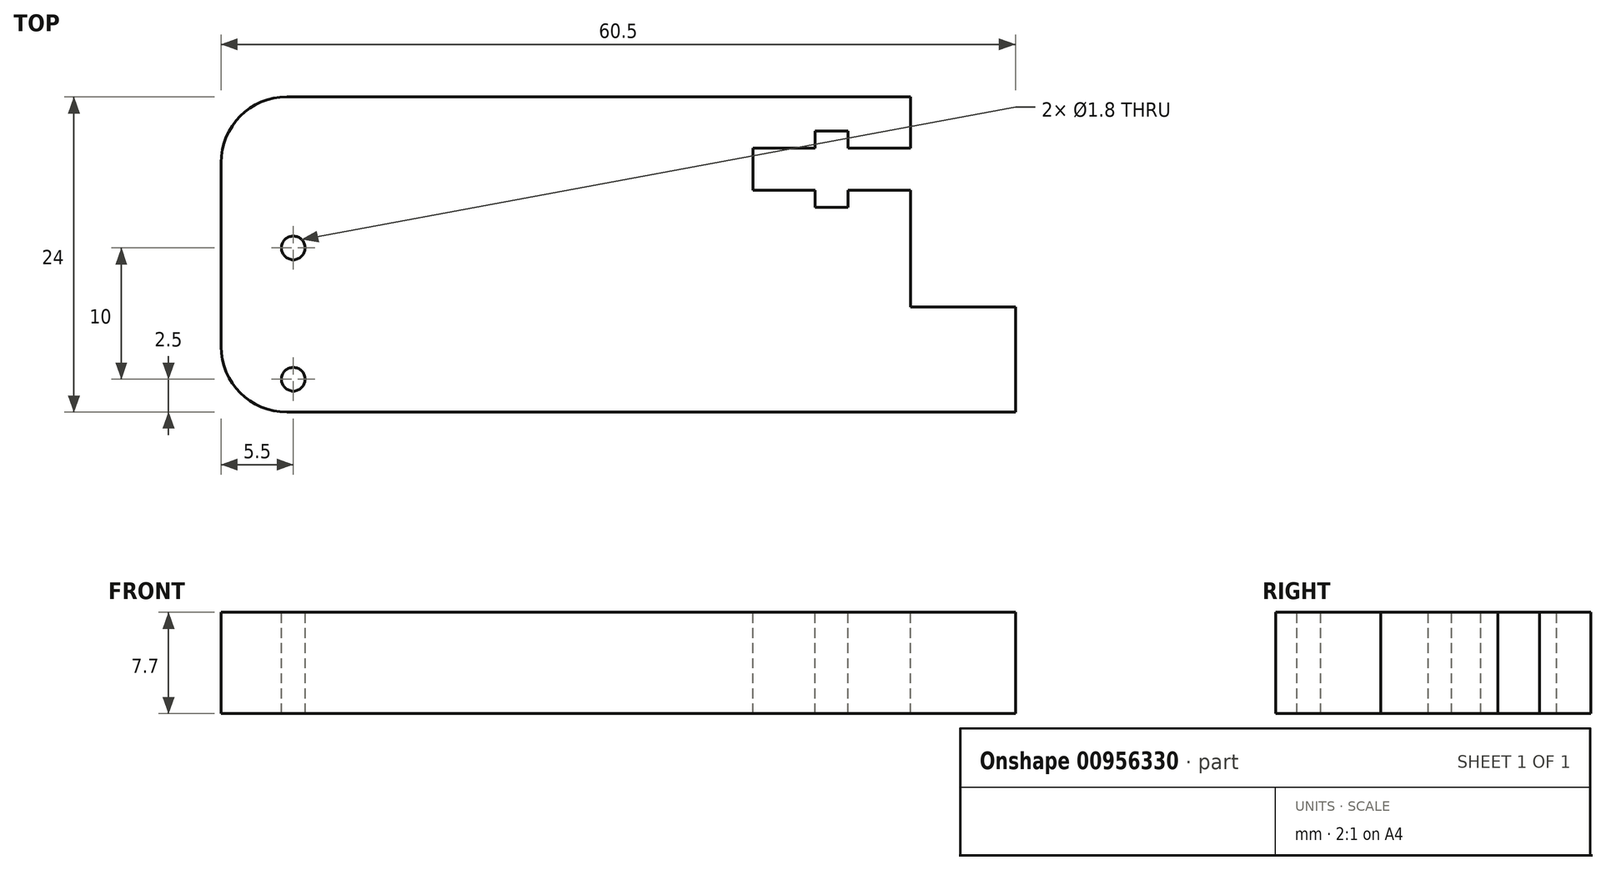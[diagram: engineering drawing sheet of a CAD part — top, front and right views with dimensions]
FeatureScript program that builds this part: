
annotation { "Feature Type Name" : "Feature", "Feature Type Description" : "" }
export const myFeature = defineFeature(function(context is Context, id is Id, definition is map)
    precondition{}
    {
        {
            var Q0;
            Q0=qCreatedBy(makeId("Top.planeOp"),FACE);
            var sketch = newSketch(context, id + "F0", { "sketchPlane" : qUnion([Q0])});
            skLineSegment(sketch, "E0", {"start": v(0, 0) * mm, "end": v(0, -8) * mm});
            skLineSegment(sketch, "E1", {"start": v(0, -8) * mm, "end": v(-60.5, -8) * mm});
            skLineSegment(sketch, "E2", {"start": v(-60.5, -8) * mm, "end": v(-60.5, 16) * mm});
            skLineSegment(sketch, "E3", {"start": v(-60.5, 16) * mm, "end": v(-8, 16) * mm});
            skLineSegment(sketch, "E4", {"start": v(-8, 16) * mm, "end": v(-8, 0) * mm});
            skLineSegment(sketch, "E5", {"start": v(-8, 0) * mm, "end": v(0, 0) * mm});
            skSolve(sketch);
        }
        {
            var Q0;
            Q0=makeQuery(id+"F0.imprint","IMPRINT",FACE,{"disambiguationData":[TD([[makeQuery(id+"F0.imprint","IMPRINT",EDGE,{"derivedFrom":sQuery(id+"F0.wireOp",EDGE,"E0")}),-1.0]])]});
            extrude(context, id + "F1", {"entities" : qUnion([Q0]), "depth" : 7.7 * mm, "offsetDistance" : 25 * mm});
        }
        {
            var Q0;
            Q0=makeQuery(id+"F1.opExtrude","CAP_FACE",FACE,{"disambiguationData":[OSD([sQuery(id+"F0.wireOp",EDGE,"E0"),sQuery(id+"F0.wireOp",EDGE,"E1"),sQuery(id+"F0.wireOp",EDGE,"E2"),sQuery(id+"F0.wireOp",EDGE,"E3"),sQuery(id+"F0.wireOp",EDGE,"E4"),sQuery(id+"F0.wireOp",EDGE,"E5")])],"isStart":false});
            var sketch = newSketch(context, id + "F2", { "sketchPlane" : qUnion([Q0])});
            skLineSegment(sketch, "E6", {"start": v(-8, 8.9) * mm, "end": v(-12.75, 8.9) * mm});
            skLineSegment(sketch, "E7", {"start": v(-12.75, 8.9) * mm, "end": v(-12.75, 7.6) * mm});
            skLineSegment(sketch, "E8", {"start": v(-12.75, 7.6) * mm, "end": v(-15.25, 7.6) * mm});
            skLineSegment(sketch, "E9", {"start": v(-15.25, 7.6) * mm, "end": v(-15.25, 8.9) * mm});
            skLineSegment(sketch, "E10", {"start": v(-15.25, 8.9) * mm, "end": v(-20, 8.9) * mm});
            skLineSegment(sketch, "E11", {"start": v(-20, 8.9) * mm, "end": v(-20, 12.1) * mm});
            skLineSegment(sketch, "E12", {"start": v(-20, 12.1) * mm, "end": v(-15.25, 12.1) * mm});
            skLineSegment(sketch, "E13", {"start": v(-15.25, 12.1) * mm, "end": v(-15.25, 13.4) * mm});
            skLineSegment(sketch, "E14", {"start": v(-15.25, 13.4) * mm, "end": v(-12.75, 13.4) * mm});
            skLineSegment(sketch, "E15", {"start": v(-12.75, 13.4) * mm, "end": v(-12.75, 12.1) * mm});
            skLineSegment(sketch, "E16", {"start": v(-12.75, 12.1) * mm, "end": v(-8, 12.1) * mm});
            skCircle(sketch, "E17", {"center": v(-55, 4.5) * mm, "radius": 0.9 * mm});
            skCircle(sketch, "E18", {"center": v(-55, -5.5) * mm, "radius": 0.9 * mm});
            skLineSegment(sketch, "E19", {"start": v(-55, -5.5) * mm, "end": v(-55, 4.5) * mm, "construction": true});
            skLineSegment(sketch, "E20", {"start": v(-55, -5.5) * mm, "end": v(-60.5, -5.5) * mm, "construction": true});
            skLineSegment(sketch, "E21", {"start": v(-55, -5.5) * mm, "end": v(-55, -8) * mm, "construction": true});
            skSolve(sketch);
        }
        {
            var Q0;
            Q0=makeQuery(id+"F2.imprint","IMPRINT",FACE,{"disambiguationData":[TD([[makeQuery(id+"F2.imprint","IMPRINT",EDGE,{"derivedFrom":sQuery(id+"F2.wireOp",EDGE,"E17")}),1.0]])]});
            var Q1;
            Q1=makeQuery(id+"F2.imprint","IMPRINT",FACE,{"disambiguationData":[TD([[makeQuery(id+"F2.imprint","IMPRINT",EDGE,{"derivedFrom":sQuery(id+"F2.wireOp",EDGE,"E18")}),1.0]])]});
            var Q2;
            {var subQ0=sQuery(id+"F2.wireOp",EDGE,"E6");Q2=makeQuery(id+"F2.imprint","IMPRINT",FACE,{"disambiguationData":[TD([[makeQuery(id+"F2.imprint","IMPRINT",EDGE,{"derivedFrom":subQ0}),-1.0]])]});}
            var Q3;
            Q3=makeQuery(id+"F1.opExtrude","CAP_FACE",FACE,{"disambiguationData":[OSD([sQuery(id+"F0.wireOp",EDGE,"E0"),sQuery(id+"F0.wireOp",EDGE,"E1"),sQuery(id+"F0.wireOp",EDGE,"E2"),sQuery(id+"F0.wireOp",EDGE,"E3"),sQuery(id+"F0.wireOp",EDGE,"E4"),sQuery(id+"F0.wireOp",EDGE,"E5")])],"isStart":true});
            extrude(context, id + "F3", {"entities" : qUnion([Q0, Q1, Q2]), "operationType" : NewBodyOperationType.REMOVE, "endBound" : BoundingType.UP_TO_SURFACE, "oppositeDirection" : true, "depth" : 25 * mm, "endBoundEntityFace" : qUnion([Q3]), "offsetDistance" : 25 * mm});
        }
        {
            var Q0;
            Q0=makeQuery(id+"F1.opExtrude","SWEPT_EDGE",EDGE,{"disambiguationData":[OSD([sQuery(id+"F0.wireOp",EDGE,"E2"),sQuery(id+"F0.wireOp",EDGE,"E3")])]});
            var Q1;
            Q1=makeQuery(id+"F1.opExtrude","SWEPT_EDGE",EDGE,{"disambiguationData":[OSD([sQuery(id+"F0.wireOp",EDGE,"E1"),sQuery(id+"F0.wireOp",EDGE,"E2")])]});
            fillet(context, id + "F4", {"entities" : qUnion([Q0, Q1]), "radius" : 5 * mm, "tangentPropagation" : true, "allowEdgeOverflow" : false});
        }
    });
